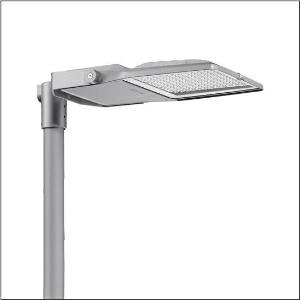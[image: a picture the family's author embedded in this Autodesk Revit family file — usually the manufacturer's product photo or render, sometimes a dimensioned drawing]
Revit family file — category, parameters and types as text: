
# Revit family: floodlight_fl_21_iq_midi___pl52_5xa7781f4d3a_7000
name_source: partatom
category: Lighting Fixtures
units: mm (PartAtom-declared; Revit-internal decimal feet)

## family parameters
Cut with Voids When Loaded = No
Host = Face
Light Source = No
Part Type = Normal
Room Calculation Point = No
Round Connector Dimension = Use Diameter
Shared = No

## types (1)
- --- (1 x LED, 37330 lm, 270.2 W, 4000K)
    Apparent Load = 270 VA
    CIE Flux Codes = 26 60 98 100 100
    Color Rendering = 70
    Color Temperature = 4000K
    Default Elevation = 1800 mm
    Description = Floodlight FL 21 iQ midi, floodlight, primary light control with lens, of PMMA, primary optical cover: protective disc, of toughened safety glass, transparent, light distribution: PL52, light emission: direct distribution, installation type: surface-mounted, LED, High Power LED, rated luminous flux: 37.330lm, luminous efficacy: 138lm/W, light colour: 740, colour temperature: 4000K, control gear: ECG iQ, control: optimised constant luminous flux control (CLO 2.0), Desk-Remote (wireless, voltage-free reading and setting of iQ features in the workshop via application-optimized NFC function/RFID function), Light-Fading, Smart-Wire, Night-Set, Lumen-Switch, Temp-Guard, Auto-Match, with terminal, 6-pole, mains connection: 220..240V, AC, 50/60Hz, start of lifetime: 270W, end of service life: 287W, reduction: 118W, luminaire housing, of diecast aluminium, powder-coated, Siteco® metallic grey (DB 702S), corrosivity category C5 mid according to DIN EN ISO 12944, sealing non-destructively replaceable, please order mast flange separately, mast bracket, of steel, galvanised, powder-coated, Siteco® metallic grey (DB 702S), protection rating (complete): IP66, insulation class (complete): insulation class II (safety insulation), certification: CE, protection symbol: D, impact resistance: IK08, permissible operating ambient temperature: -40..+40°C, permissible operating ambient temperature for outdoor applications: -40..+50°C, standard: DIN EN 12944, LABS conformity tested according to VDMA 24364:2018-05, packaging unit: 1 piece

Light Distribution: PL52
    Height = 76 mm
    Lamp = 1 x LED
    Lamp Light Flux = 37330 lm
    Lamp Power = 270.2 W
    Lamp count = 1
    Length = 657 mm
    Luminous efficacy = 138 lm/W
    Manufacturer = Siteco
    ModVariant = No
    Model = 5XA7781F4D3A
    Number of Poles = 1
    OnlyDefault = Yes
    Power Factor = 1
    Product Name = Floodlight FL 21 iQ midi | PL52
    Product group = floodlight | pylon annexe
    ProductGroupID = 6200
    Protection Class = Protection class II
    Protection Degree = IP 66
    RLX_Detail_Level = 1
    RLX_Emergency_Light_Flux = 0 lm
    RLX_Emergency_Type = 0
    RLX_Emergency_Type_DB = No
    RlxData = <blob elided: 153609 chars, md5=da9fefee>
    Socket = socket
    Standby Power = 0 W
    System Light Flux = 37330 lm
    System Power = 270 W
    Type Comments = factory setting: luminous flux: 100 % | dim-lin: 254 | 620 mA
    Type Image = l_1007123.jpg
    URL = http://relux.com
    VarID = @adj_054035
    Voltage = 0 V
    Weight = 0.00 kg
    Width = 442 mm

## geometry (parser evidence)
native form markers: Blend x4, Sweep x15
no freeform markers — native parametric forms only
